# Revit family: Deckel rastbar- DGRR 50_100_150_200_300_400_500_600_FS_FT
name_source: partatom
category: Generic Models
revit_build: Autodesk Revit 2017 (Build: 20190508_0315(x64)
units: mm (PartAtom-declared; Revit-internal decimal feet)

## family parameters
Always vertical = Yes
Can host rebar = No
Cut with Voids When Loaded = No
Part Type = Normal
Room Calculation Point = No
Round Connector Dimension = Use Diameter
Shared = No
Work Plane-Based = No

## types (24) — shared parameters
Manufacturer = OBO BETTERMANN
URL = http://www.obo-bettermann.com

## per-type parameters (varying)
| type | Article Type | GTIN | Manufacturer Art.No. | Material | Width | Width 1 |
| DGRR 50 FT | DGRR 50 FT | 4012196687251 | 6001820 | Edelstahl, rostfrei A2 | 50 mm  [stored 0.164042 ft] | 25 mm  [stored 0.082021 ft] |
| DGRR 100 FT | DGRR 100 FT | 4012196687268 | 6001822 | Edelstahl, rostfrei A2 | 100 mm  [stored 0.328084 ft] | 50 mm  [stored 0.164042 ft] |
| DGRR 150 FT | DGRR 150 FT | 4012196687275 | 6001824 | Edelstahl, rostfrei A2 | 150 mm | 75 mm |
| DGRR 200 FT | DGRR 200 FT | 4012196687282 | 6001826 | Edelstahl, rostfrei A2 | 200 mm  [stored 0.656168 ft] | 100 mm  [stored 0.328084 ft] |
| DGRR 300 FT | DGRR 300 FT | 4012196687299 | 6001828 | Edelstahl, rostfrei A2 | 300 mm | 150 mm |
| DGRR 400 FT | DGRR 400 FT | 4012196687305 | 6001830 | Edelstahl, rostfrei A2 | 400 mm  [stored 1.31234 ft] | 200 mm  [stored 0.656168 ft] |
| DGRR 500 FT | DGRR 500 FT | 4012196687312 | 6001832 | Edelstahl, rostfrei A2 | 500 mm  [stored 1.64042 ft] | 250 mm  [stored 0.82021 ft] |
| DGRR 600 FT | DGRR 600 FT | 4012196687329 | 6001834 | Edelstahl, rostfrei A2 | 600 mm | 300 mm |
| DGRR 100 FS | DGRR 100 FS | 4012196687121 | 6001842 | Strip-galvanised | 100 mm  [stored 0.328084 ft] | 50 mm  [stored 0.164042 ft] |
| DGRR 150 FS | DGRR 150 FS | 4012196687138 | 6001844 | Strip-galvanised | 150 mm | 75 mm |
| DGRR 200 FS | DGRR 200 FS | 4012196687145 | 6001846 | Strip-galvanised | 200 mm  [stored 0.656168 ft] | 100 mm  [stored 0.328084 ft] |
| DGRR 300 FS | DGRR 300 FS | 4012196687152 | 6001848 | Strip-galvanised | 300 mm | 150 mm |
| DGRR 400 FS | DGRR 400 FS | 4012196687169 | 6001850 | Strip-galvanised | 400 mm  [stored 1.31234 ft] | 200 mm  [stored 0.656168 ft] |
| DGRR 600 FS | DGRR 600 FS | 4012196687183 | 6001854 | Strip-galvanised | 600 mm | 300 mm |
| DGRR 50 FS | DGRR 50 FS | 4012196687114 | 6001840 | Strip galvanised | 50 mm  [stored 0.164042 ft] | 25 mm  [stored 0.082021 ft] |
| DGRR 500 FS | DGRR 500 FS | 4012196687176 | 6001854 | Strip-galvanised | 500 mm  [stored 1.64042 ft] | 250 mm  [stored 0.82021 ft] |
| DGRR 50 A2 | DGRR 50 A2 | 4012196687190 | 6001860 | Edelstahl, rostfrei A2 | 50 mm  [stored 0.164042 ft] | 25 mm  [stored 0.082021 ft] |
| DGRR 100 A2 | DGRR 150 A2 | 4012196687206 | 6001864 | Edelstahl, rostfrei A2 | 150 mm | 75 mm |
| DGRR 150 A2 | DGRR 200 A2 | 4012196687213 | 6001866 | Edelstahl, rostfrei A2 | 150 mm | 75 mm |
| DGRR 200 A2 | DGRR 200 A2 | 4012196687848 | 6001868 | Edelstahl, rostfrei A2 | 200 mm  [stored 0.656168 ft] | 100 mm  [stored 0.328084 ft] |
| DGRR 300 A2 | DGRR 400 A2 | 4012196687220 | 6001870 | Edelstahl, rostfrei A2 | 300 mm | 150 mm |
| DGRR 400 A2 | DGRR 500 A2 | 4012196687855 | 6001872 | Edelstahl, rostfrei A2 | 400 mm  [stored 1.31234 ft] | 200 mm  [stored 0.656168 ft] |
| DGRR 500 A2 | DGRR 600 A2 | 4012196687855 | 6001874 | Edelstahl, rostfrei A2 | 600 mm | 300 mm |
| DGRR 600 A2 | DGRR 600 A2 | 4012196687855 | 6001874 | Edelstahl, rostfrei A2 | 600 mm | 300 mm |

note: [stored X ft] marks values corroborated as IEEE doubles in the binary element streams (Revit-internal decimal feet)

## geometry (parser evidence)
native form markers: Sweep x3
no freeform markers — native parametric forms only
